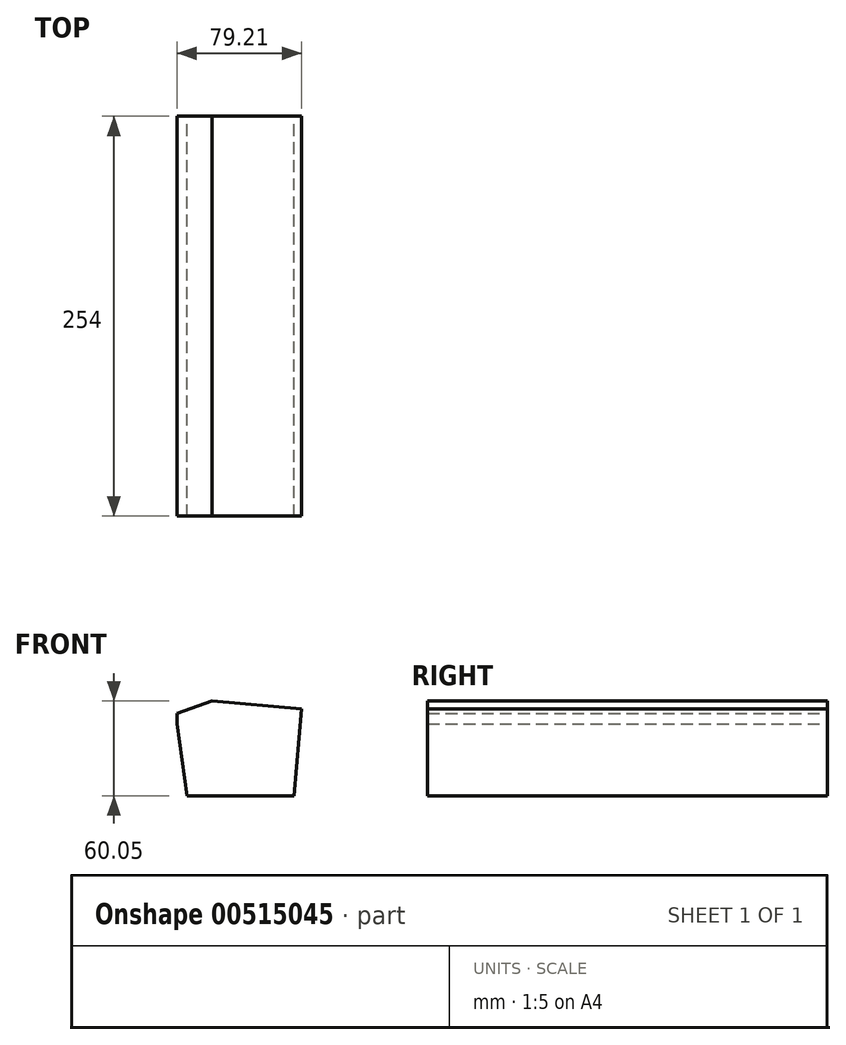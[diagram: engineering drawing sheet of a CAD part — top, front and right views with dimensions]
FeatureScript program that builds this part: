
annotation { "Feature Type Name" : "Feature", "Feature Type Description" : "" }
export const myFeature = defineFeature(function(context is Context, id is Id, definition is map)
    precondition{}
    {
        {
            var Q0;
            Q0=qCreatedBy(makeId("Front.planeOp"),FACE);
            var sketch = newSketch(context, id + "F0", { "sketchPlane" : qUnion([Q0])});
            skLineSegment(sketch, "E0", {"start": v(-12.81, 36.45) * mm, "end": v(-12.81, 29.6) * mm});
            skLineSegment(sketch, "E1", {"start": v(-12.81, 29.6) * mm, "end": v(-6.32, -15.88) * mm});
            skLineSegment(sketch, "E2", {"start": v(-6.32, -15.88) * mm, "end": v(61.71, -15.88) * mm});
            skLineSegment(sketch, "E3", {"start": v(61.71, -15.88) * mm, "end": v(66.4, 39.34) * mm});
            skLineSegment(sketch, "E4", {"start": v(66.4, 39.34) * mm, "end": v(9.53, 44.17) * mm});
            skLineSegment(sketch, "E5", {"start": v(9.53, 44.17) * mm, "end": v(-12.81, 36.45) * mm});
            skSolve(sketch);
        }
        {
            var Q0;
            Q0 = qSketchRegion(id + "F0", true);
            extrude(context, id + "F1", {"entities" : qUnion([Q0]), "endBound" : BoundingType.SYMMETRIC, "depth" : 254 * mm, "offsetDistance" : 25.4 * mm});
        }
    });
